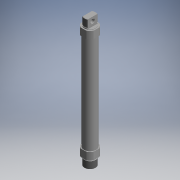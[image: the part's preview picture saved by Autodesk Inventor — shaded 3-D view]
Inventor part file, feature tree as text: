
AUTODESK INVENTOR PART (.ipt)
format: ipt  version: 2017.3 (Build 213256000, 256)  size: 245,760 bytes
history: native  units: mm (DEFAULTED — no unit token found)
features: other x70, sketch x7, revolve x3, thread x2, extrude x2, hole x2
ambient origin geometry x8: Origin, YZ Plane, XZ Plane, XY Plane, X Axis, Y Axis, Z Axis, Center Point
bodies: Solid1 (feature_tree)
feature tree (86):
  revolve  "Revolution1"  [1 undecoded]
  thread  "Thread1"  [1 undecoded]
  thread  "Thread2"  [1 undecoded]
  extrude  "Extrusion1"  TaperAngle=360.0deg  [1 undecoded]
  extrude  "Extrusion2"  TaperAngle=360.0deg  [1 undecoded]
  revolve  "Revolution2"  [1 undecoded]
  hole  "Hole1"  [1 undecoded]
  hole  "Hole2"  [1 undecoded]
  revolve  "Revolution3"  [1 undecoded]
  other  "FDT_FRONT_XY"
  other  "FDT_FRONT_YZ"
  other  "FDT_FRONT_ZX"
  other  "FDT_FRONT_X"
  other  "FDT_FRONT_Y"
  other  "FDT_FRONT_Z"
  other  "FDT_FRONT_Center"
  other  "FDT_QSFRONT_XY"
  other  "FDT_QSFRONT_YZ"
  other  "FDT_QSFRONT_ZX"
  other  "FDT_QSFRONT_X"
  other  "FDT_QSFRONT_Y"
  other  "FDT_QSFRONT_Z"
  other  "FDT_QSFRONT_Center"
  other  "FDT_QSREAR_XY"
  other  "FDT_QSREAR_YZ"
  other  "FDT_QSREAR_ZX"
  other  "FDT_QSREAR_X"
  other  "FDT_QSREAR_Y"
  other  "FDT_QSREAR_Z"
  other  "FDT_QSREAR_Center"
  other  "FDT_REAR_XY"
  other  "FDT_REAR_YZ"
  other  "FDT_REAR_ZX"
  other  "FDT_REAR_X"
  other  "FDT_REAR_Y"
  other  "FDT_REAR_Z"
  other  "FDT_REAR_Center"
  other  "FDT_SMBR1_XY"
  other  "FDT_SMBR1_YZ"
  other  "FDT_SMBR1_ZX"
  other  "FDT_SMBR1_X"
  other  "FDT_SMBR1_Y"
  other  "FDT_SMBR1_Z"
  other  "FDT_SMBR1_Center"
  other  "FDT_SMBR2_XY"
  other  "FDT_SMBR2_YZ"
  other  "FDT_SMBR2_ZX"
  other  "FDT_SMBR2_X"
  other  "FDT_SMBR2_Y"
  other  "FDT_SMBR2_Z"
  other  "FDT_SMBR2_Center"
  other  "FDT_SWIVELAXIS_XY"
  other  "FDT_SWIVELAXIS_YZ"
  other  "FDT_SWIVELAXIS_ZX"
  other  "FDT_SWIVELAXIS_X"
  other  "FDT_SWIVELAXIS_Y"
  other  "FDT_SWIVELAXIS_Z"
  other  "FDT_SWIVELAXIS_Center"
  other  "NUT_XY"
  other  "NUT_YZ"
  other  "NUT_ZX"
  other  "NUT_X"
  other  "NUT_Y"
  other  "NUT_Z"
  other  "NUT_Center"
  other  "ZR_XY"
  other  "ZR_YZ"
  other  "ZR_ZX"
  other  "ZR_X"
  other  "ZR_Y"
  other  "ZR_Z"
  other  "ZR_Center"
  other  "ZYL_XY"
  other  "ZYL_YZ"
  other  "ZYL_ZX"
  other  "ZYL_X"
  other  "ZYL_Y"
  other  "ZYL_Z"
  other  "ZYL_Center"
  sketch  "Sketch_12"  dims[d25=0.0mm d26=0.0mm d27=0.0mm d28=0.0mm d29=0.0mm d30=0.0mm]
  sketch  "Sketch_1"  dims[d0=360.0deg d1=23.03mm d2=0.0mm d3=23.03mm d4=0.0mm d5=453.6mm d6=0.0mm]
  sketch  "Sketch_124"
  sketch  "Sketch_3"  dims[d7=46.0mm d8=0.0mm d9=360.0deg]
  sketch  "Sketch5"  dims[d10=11.445mm d11=15.856mm d12=13.157mm d13=2.0mm d14=90.0deg d15=22.5mm d16=0.0mm]
  sketch  "Sketch6"  dims[d17=11.445mm d18=9.856mm d19=13.157mm d20=2.0mm d21=90.0deg d22=10.5mm d23=120.0deg d24=360.0deg]
  sketch  "Sketch_129"
note: 9 required parameter values undecoded (feature->parameter linkage not recoverable at this tier; creation-order binding heuristic only, values carry confidence <= 0.55)